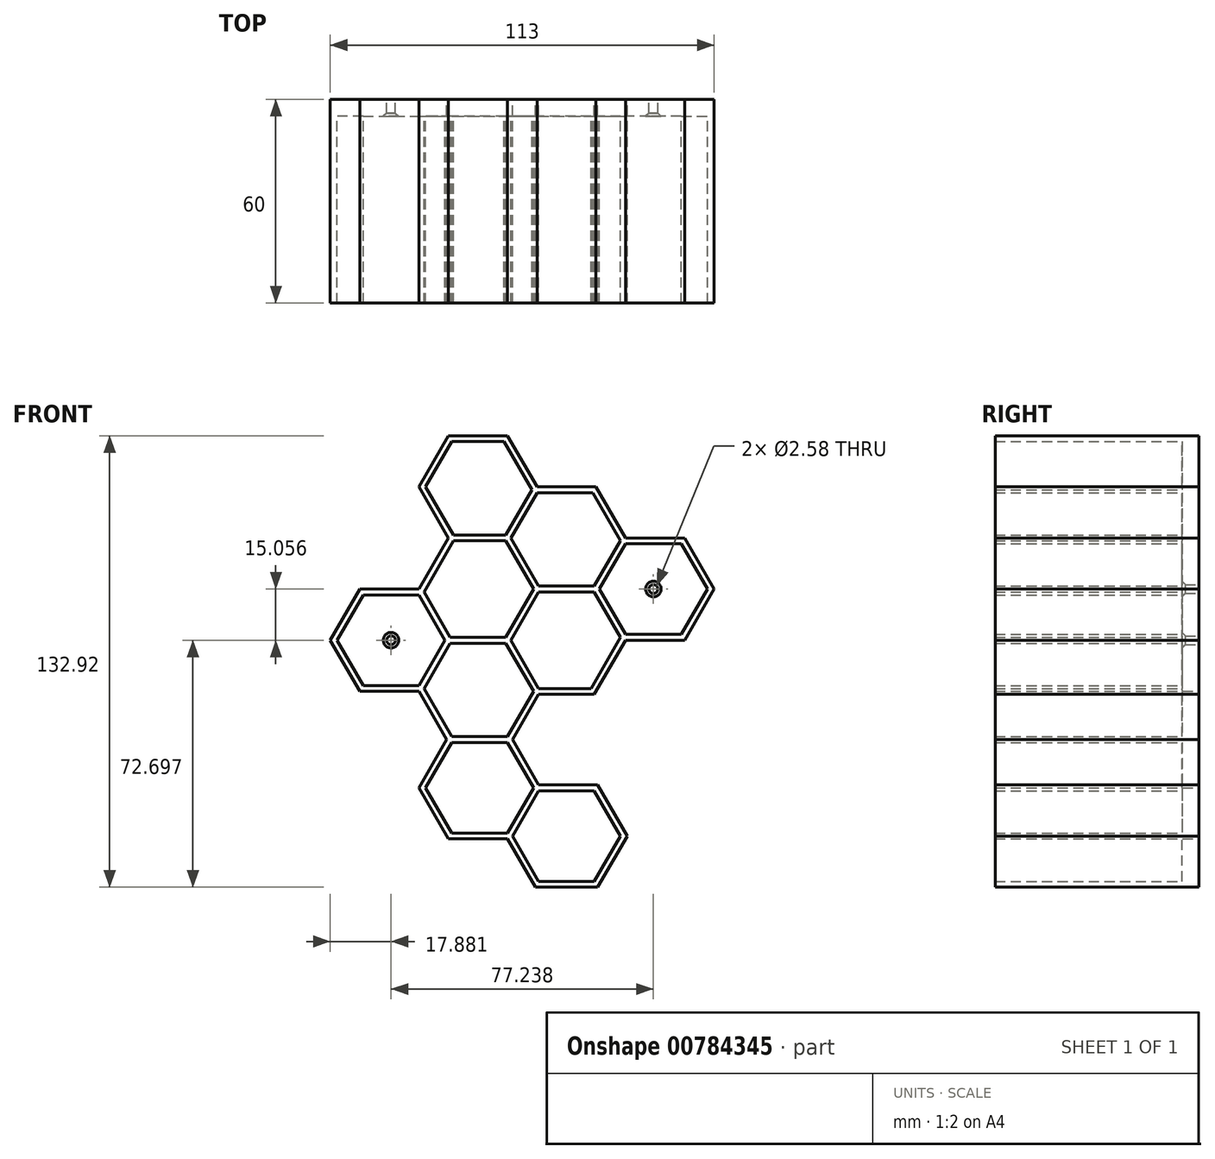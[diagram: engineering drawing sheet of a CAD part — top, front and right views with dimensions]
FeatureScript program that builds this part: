
annotation { "Feature Type Name" : "Feature", "Feature Type Description" : "" }
export const myFeature = defineFeature(function(context is Context, id is Id, definition is map)
    precondition{}
    {
        {
            var Q0;
            Q0=qCreatedBy(makeId("Front.planeOp"),FACE);
            var sketch = newSketch(context, id + "F0", { "sketchPlane" : qUnion([Q0])});
            skLineSegment(sketch, "E0.2", {"start": v(-21.73, -39.87) * mm, "end": v(-30.42, -24.82) * mm});
            skLineSegment(sketch, "E1.3", {"start": v(-30.42, 5.3) * mm, "end": v(-21.73, 20.35) * mm});
            skPoint(sketch, "E1.0.midPoint", {"position": v(0, -2.23) * mm});
            skLineSegment(sketch, "E2.3", {"start": v(30.42, -9.76) * mm, "end": v(21.73, -24.82) * mm});
            skLineSegment(sketch, "E3.4", {"start": v(4.35, 35.4) * mm, "end": v(21.73, 35.4) * mm});
            skLineSegment(sketch, "E3.5", {"start": v(21.73, 35.4) * mm, "end": v(30.42, 20.35) * mm});
            skLineSegment(sketch, "E4.0", {"start": v(56.5, 5.3) * mm, "end": v(47.8, -9.76) * mm});
            skLineSegment(sketch, "E4.1", {"start": v(47.8, -9.76) * mm, "end": v(30.42, -9.76) * mm});
            skLineSegment(sketch, "E4.4", {"start": v(30.42, 20.35) * mm, "end": v(47.8, 20.35) * mm});
            skLineSegment(sketch, "E4.5", {"start": v(47.8, 20.35) * mm, "end": v(56.5, 5.3) * mm});
            skLineSegment(sketch, "E5.2", {"start": v(-21.73, 20.35) * mm, "end": v(-30.42, 35.4) * mm});
            skLineSegment(sketch, "E5.3", {"start": v(-30.42, 35.4) * mm, "end": v(-21.73, 50.46) * mm});
            skLineSegment(sketch, "E5.4", {"start": v(-21.73, 50.46) * mm, "end": v(-4.35, 50.46) * mm});
            skLineSegment(sketch, "E5.5", {"start": v(-4.35, 50.46) * mm, "end": v(4.35, 35.4) * mm});
            skLineSegment(sketch, "E6.2", {"start": v(-30.42, -24.82) * mm, "end": v(-47.8, -24.82) * mm});
            skLineSegment(sketch, "E6.3", {"start": v(-47.8, -24.82) * mm, "end": v(-56.5, -9.76) * mm});
            skLineSegment(sketch, "E6.4", {"start": v(-56.5, -9.76) * mm, "end": v(-47.8, 5.3) * mm});
            skLineSegment(sketch, "E6.5", {"start": v(-47.8, 5.3) * mm, "end": v(-30.42, 5.3) * mm});
            skLineSegment(sketch, "E7.0", {"start": v(-28.44, 35.4) * mm, "end": v(-20.74, 48.74) * mm});
            skLineSegment(sketch, "E7.3", {"start": v(-46.81, 3.57) * mm, "end": v(-30.42, 3.57) * mm});
            skLineSegment(sketch, "E7.4", {"start": v(-54.51, -9.76) * mm, "end": v(-46.81, 3.57) * mm});
            skLineSegment(sketch, "E7.5", {"start": v(-20.74, 48.74) * mm, "end": v(-5.34, 48.74) * mm});
            skLineSegment(sketch, "E7.6", {"start": v(-46.81, -23.1) * mm, "end": v(-54.51, -9.76) * mm});
            skLineSegment(sketch, "E7.8", {"start": v(-20.74, -38.15) * mm, "end": v(-28.93, -23.96) * mm});
            skLineSegment(sketch, "E7.13", {"start": v(20.74, 33.68) * mm, "end": v(28.93, 19.49) * mm});
            skLineSegment(sketch, "E7.15", {"start": v(-5.34, 48.74) * mm, "end": v(2.86, 34.54) * mm});
            skLineSegment(sketch, "E7.16", {"start": v(46.81, 18.63) * mm, "end": v(54.51, 5.3) * mm});
            skLineSegment(sketch, "E7.17", {"start": v(54.51, 5.3) * mm, "end": v(46.81, -8.04) * mm});
            skLineSegment(sketch, "E7.18", {"start": v(46.81, -8.04) * mm, "end": v(30.42, -8.04) * mm});
            skLineSegment(sketch, "E8.2", {"start": v(3.35, 5.3) * mm, "end": v(-4.84, 19.49) * mm});
            skLineSegment(sketch, "E8.3", {"start": v(3.35, 5.3) * mm, "end": v(-4.84, -8.9) * mm});
            skLineSegment(sketch, "E8.4", {"start": v(-4.84, -8.9) * mm, "end": v(-21.23, -8.9) * mm});
            skLineSegment(sketch, "E9.0", {"start": v(-4.84, 21.2) * mm, "end": v(2.86, 34.54) * mm});
            skLineSegment(sketch, "E10.0", {"start": v(-3.35, 20.35) * mm, "end": v(4.35, 33.68) * mm});
            skLineSegment(sketch, "E10.1", {"start": v(4.84, 6.15) * mm, "end": v(-3.35, 20.35) * mm});
            skLineSegment(sketch, "E10.2", {"start": v(4.84, 6.15) * mm, "end": v(21.23, 6.15) * mm});
            skLineSegment(sketch, "E10.3", {"start": v(21.23, 6.15) * mm, "end": v(28.93, 19.49) * mm});
            skLineSegment(sketch, "E11.0", {"start": v(22.72, 5.3) * mm, "end": v(30.42, 18.63) * mm});
            skLineSegment(sketch, "E11.1", {"start": v(22.72, 5.3) * mm, "end": v(30.42, -8.04) * mm});
            skLineSegment(sketch, "E12.0", {"start": v(21.23, 4.43) * mm, "end": v(28.93, -8.9) * mm});
            skLineSegment(sketch, "E12.2", {"start": v(-3.35, -9.76) * mm, "end": v(4.84, -23.96) * mm});
            skLineSegment(sketch, "E12.3", {"start": v(4.84, 4.43) * mm, "end": v(-3.35, -9.76) * mm});
            skLineSegment(sketch, "E12.4", {"start": v(4.84, 4.43) * mm, "end": v(21.23, 4.43) * mm});
            skLineSegment(sketch, "E13.0", {"start": v(-22.72, -9.76) * mm, "end": v(-30.42, -23.1) * mm});
            skLineSegment(sketch, "E14.0", {"start": v(-21.23, -10.62) * mm, "end": v(-28.93, -23.96) * mm});
            skLineSegment(sketch, "E14.1", {"start": v(-4.84, -10.62) * mm, "end": v(-21.23, -10.62) * mm});
            skLineSegment(sketch, "E14.2", {"start": v(-4.84, -10.62) * mm, "end": v(3.35, -24.82) * mm});
            skLineSegment(sketch, "E14.3", {"start": v(3.35, -24.82) * mm, "end": v(-4.35, -38.15) * mm});
            skLineSegment(sketch, "E15.1", {"start": v(4.84, -25.68) * mm, "end": v(20.24, -25.68) * mm});
            skPoint(sketch, "E16", {"position": v(12.8, 19.92) * mm});
            skLineSegment(sketch, "E17", {"start": v(-0.75, -1.8) * mm, "end": v(0.75, -2.67) * mm, "construction": true});
            skLineSegment(sketch, "E18", {"start": v(30.42, 18.63) * mm, "end": v(46.81, 18.63) * mm});
            skLineSegment(sketch, "E19", {"start": v(28.93, -8.9) * mm, "end": v(20.24, -23.96) * mm});
            skLineSegment(sketch, "E20", {"start": v(20.24, -23.96) * mm, "end": v(4.84, -23.96) * mm});
            skLineSegment(sketch, "E21", {"start": v(-4.35, -38.15) * mm, "end": v(-20.74, -38.15) * mm});
            skLineSegment(sketch, "E22", {"start": v(-30.42, -23.1) * mm, "end": v(-46.81, -23.1) * mm});
            skLineSegment(sketch, "E23", {"start": v(-30.42, 3.57) * mm, "end": v(-22.72, -9.76) * mm});
            skLineSegment(sketch, "E24", {"start": v(-28.93, 4.43) * mm, "end": v(-21.23, -8.9) * mm});
            skLineSegment(sketch, "E25", {"start": v(-28.93, 4.43) * mm, "end": v(-20.24, 19.49) * mm});
            skLineSegment(sketch, "E26", {"start": v(-20.24, 21.2) * mm, "end": v(-28.44, 35.4) * mm});
            skLineSegment(sketch, "E27", {"start": v(-20.24, 21.2) * mm, "end": v(-4.84, 21.2) * mm});
            skLineSegment(sketch, "E28", {"start": v(-20.24, 19.49) * mm, "end": v(-4.84, 19.49) * mm});
            skLineSegment(sketch, "E29", {"start": v(4.35, 33.68) * mm, "end": v(20.74, 33.68) * mm});
            skLineSegment(sketch, "E30", {"start": v(46.81, 18.63) * mm, "end": v(30.42, -8.04) * mm, "construction": true});
            skLineSegment(sketch, "E31", {"start": v(-30.42, 3.57) * mm, "end": v(-46.81, -23.1) * mm, "construction": true});
            skLineSegment(sketch, "E32", {"start": v(-21.23, -10.62) * mm, "end": v(-20.74, -9.76) * mm, "construction": true});
            skLineSegment(sketch, "E33", {"start": v(-21.23, -8.9) * mm, "end": v(-20.74, -9.76) * mm, "construction": true});
            skLineSegment(sketch, "E34", {"start": v(-30.42, -24.82) * mm, "end": v(-29.43, -24.82) * mm, "construction": true});
            skLineSegment(sketch, "E35", {"start": v(-28.44, -24.82) * mm, "end": v(-28.93, -23.96) * mm, "construction": true});
            skLineSegment(sketch, "E36", {"start": v(-28.93, -23.96) * mm, "end": v(-29.43, -24.82) * mm, "construction": true});
            skPoint(sketch, "E37", {"position": v(-29.43, -24.82) * mm});
            skPoint(sketch, "E38", {"position": v(-20.74, -9.76) * mm});
            skLineSegment(sketch, "E39", {"start": v(-20.74, -9.76) * mm, "end": v(-20.24, -10.62) * mm, "construction": true});
            skLineSegment(sketch, "E40", {"start": v(-20.74, -9.76) * mm, "end": v(-20.24, -8.9) * mm, "construction": true});
            skLineSegment(sketch, "E41", {"start": v(-29.43, -24.82) * mm, "end": v(-28.44, -24.82) * mm, "construction": true});
            skLineSegment(sketch, "E42", {"start": v(-29.43, -24.82) * mm, "end": v(-29.93, -25.68) * mm, "construction": true});
            skLineSegment(sketch, "E43", {"start": v(-30.42, 5.3) * mm, "end": v(-29.43, 5.3) * mm, "construction": true});
            skLineSegment(sketch, "E44", {"start": v(-28.93, 4.43) * mm, "end": v(-29.93, 6.15) * mm, "construction": true});
            skLineSegment(sketch, "E45", {"start": v(-29.43, 5.3) * mm, "end": v(-28.44, 5.3) * mm, "construction": true});
            skLineSegment(sketch, "E46", {"start": v(20.24, -25.68) * mm, "end": v(21.23, -25.68) * mm});
            skLineSegment(sketch, "E47", {"start": v(21.73, -24.82) * mm, "end": v(21.23, -25.68) * mm});
            skPoint(sketch, "E48", {"position": v(-3.27, -37.05) * mm});
            skLineSegment(sketch, "E49", {"start": v(-4.35, -38.15) * mm, "end": v(-3.35, -39.87) * mm, "construction": true});
            skLineSegment(sketch, "E50", {"start": v(-47.8, 5.3) * mm, "end": v(-46.81, 3.57) * mm, "construction": true});
            skLineSegment(sketch, "E51", {"start": v(-21.73, -39.87) * mm, "end": v(-3.35, -39.87) * mm});
            skLineSegment(sketch, "E52", {"start": v(-3.35, -39.87) * mm, "end": v(4.84, -25.68) * mm});
            skPoint(sketch, "E53", {"position": v(-13.94, -39.01) * mm});
            skLineSegment(sketch, "E54", {"start": v(-13.94, -39.01) * mm, "end": v(-22.23, -39.01) * mm, "construction": true});
            skLineSegment(sketch, "E55", {"start": v(-13.94, -39.01) * mm, "end": v(-2.86, -39.01) * mm, "construction": true});
            skLineSegment(sketch, "E56.2", {"start": v(-4.35, -68.26) * mm, "end": v(-21.73, -68.26) * mm});
            skLineSegment(sketch, "E56.3", {"start": v(-21.73, -68.26) * mm, "end": v(-30.42, -53.2) * mm});
            skLineSegment(sketch, "E56.4", {"start": v(-30.42, -53.2) * mm, "end": v(-21.73, -38.15) * mm});
            skLineSegment(sketch, "E56.5", {"start": v(-21.73, -38.15) * mm, "end": v(-4.35, -38.15) * mm});
            skLineSegment(sketch, "E57.3", {"start": v(-20.74, -39.87) * mm, "end": v(-4.35, -39.87) * mm});
            skLineSegment(sketch, "E57.4", {"start": v(-28.44, -53.2) * mm, "end": v(-20.74, -39.87) * mm});
            skLineSegment(sketch, "E57.6", {"start": v(-20.74, -66.54) * mm, "end": v(-28.44, -53.2) * mm});
            skLineSegment(sketch, "E58.0", {"start": v(3.35, -53.2) * mm, "end": v(-4.35, -66.54) * mm});
            skLineSegment(sketch, "E59.0", {"start": v(4.84, -54.07) * mm, "end": v(-2.86, -67.4) * mm});
            skLineSegment(sketch, "E60", {"start": v(-4.35, -66.54) * mm, "end": v(-20.74, -66.54) * mm});
            skLineSegment(sketch, "E61", {"start": v(-4.35, -39.87) * mm, "end": v(3.35, -53.2) * mm});
            skLineSegment(sketch, "E62", {"start": v(-2.86, -39.01) * mm, "end": v(4.84, -52.35) * mm});
            skLineSegment(sketch, "E63", {"start": v(-4.43, -42.7) * mm, "end": v(-20.82, -69.36) * mm, "construction": true});
            skLineSegment(sketch, "E64", {"start": v(4.84, -54.07) * mm, "end": v(5.34, -53.2) * mm});
            skLineSegment(sketch, "E65", {"start": v(4.84, -52.35) * mm, "end": v(5.34, -53.2) * mm});
            skLineSegment(sketch, "E66", {"start": v(-4.35, -68.26) * mm, "end": v(-3.35, -68.26) * mm});
            skLineSegment(sketch, "E67", {"start": v(-2.86, -67.4) * mm, "end": v(-3.35, -68.26) * mm});
            skLineSegment(sketch, "E68", {"start": v(-4.35, -38.15) * mm, "end": v(-3.35, -38.15) * mm});
            skLineSegment(sketch, "E69", {"start": v(-2.86, -39.01) * mm, "end": v(-3.35, -38.15) * mm});
            skPoint(sketch, "E70", {"position": v(-22.23, -39.01) * mm});
            skLineSegment(sketch, "E71", {"start": v(-22.23, -39.01) * mm, "end": v(-2.86, -39.01) * mm, "construction": true});
            skLineSegment(sketch, "E72", {"start": v(4.84, -52.35) * mm, "end": v(-4.35, -68.26) * mm, "construction": true});
            skLineSegment(sketch, "E73.2", {"start": v(21.23, -82.46) * mm, "end": v(3.85, -82.46) * mm});
            skLineSegment(sketch, "E73.3", {"start": v(3.85, -82.46) * mm, "end": v(-4.84, -67.4) * mm});
            skLineSegment(sketch, "E73.4", {"start": v(-4.84, -67.4) * mm, "end": v(3.85, -52.35) * mm});
            skLineSegment(sketch, "E73.5", {"start": v(3.85, -52.35) * mm, "end": v(21.23, -52.35) * mm});
            skLineSegment(sketch, "E74.3", {"start": v(4.84, -54.07) * mm, "end": v(21.23, -54.07) * mm});
            skLineSegment(sketch, "E74.4", {"start": v(-2.86, -67.4) * mm, "end": v(4.84, -54.07) * mm});
            skLineSegment(sketch, "E74.6", {"start": v(4.84, -80.74) * mm, "end": v(-2.86, -67.4) * mm});
            skLineSegment(sketch, "E75.0", {"start": v(28.93, -67.4) * mm, "end": v(21.23, -80.74) * mm});
            skLineSegment(sketch, "E76.0", {"start": v(30.42, -68.26) * mm, "end": v(22.72, -81.6) * mm});
            skLineSegment(sketch, "E77", {"start": v(21.23, -80.74) * mm, "end": v(4.84, -80.74) * mm});
            skLineSegment(sketch, "E78", {"start": v(21.23, -54.07) * mm, "end": v(28.93, -67.4) * mm});
            skLineSegment(sketch, "E79", {"start": v(22.72, -53.2) * mm, "end": v(30.42, -66.54) * mm});
            skLineSegment(sketch, "E80", {"start": v(21.23, -54.07) * mm, "end": v(4.84, -80.74) * mm, "construction": true});
            skLineSegment(sketch, "E81", {"start": v(30.42, -68.26) * mm, "end": v(30.92, -67.4) * mm});
            skLineSegment(sketch, "E82", {"start": v(30.42, -66.54) * mm, "end": v(30.92, -67.4) * mm});
            skLineSegment(sketch, "E83", {"start": v(21.23, -82.46) * mm, "end": v(22.23, -82.46) * mm});
            skLineSegment(sketch, "E84", {"start": v(22.72, -81.6) * mm, "end": v(22.23, -82.46) * mm});
            skLineSegment(sketch, "E85", {"start": v(21.23, -52.35) * mm, "end": v(22.23, -52.35) * mm});
            skLineSegment(sketch, "E86", {"start": v(22.72, -53.2) * mm, "end": v(22.23, -52.35) * mm});
            skLineSegment(sketch, "E87", {"start": v(-4.35, -66.54) * mm, "end": v(-5.34, -68.26) * mm, "construction": true});
            skPoint(sketch, "E88", {"position": v(4.84, -52.35) * mm});
            skPoint(sketch, "E89", {"position": v(-4.35, -68.26) * mm});
            skPoint(sketch, "E90", {"position": v(-38.62, -9.76) * mm});
            skPoint(sketch, "E91", {"position": v(38.62, 5.3) * mm});
            skCircle(sketch, "E92", {"center": v(38.62, 5.3) * mm, "radius": 1.3 * mm});
            skCircle(sketch, "E93", {"center": v(-38.62, -9.76) * mm, "radius": 1.3 * mm});
            skSolve(sketch);
        }
        {
            var Q0;
            Q0=makeQuery(id+"F0.imprint","IMPRINT",FACE,{"disambiguationData":[TD([[makeQuery(id+"F0.imprint","IMPRINT",EDGE,{"derivedFrom":sQuery(id+"F0.wireOp",EDGE,"E1.3")}),-1.0]])]});
            var Q1;
            {var subQ2=sQuery(id+"F0.wireOp",EDGE,"E61");Q1=makeQuery(id+"F0.imprint","IMPRINT",FACE,{"disambiguationData":[TD([[makeQuery(id+"F0.imprint","IMPRINT",EDGE,{"derivedFrom":subQ2}),1.0]])]});}
            var Q2;
            Q2=makeQuery(id+"F0.imprint","IMPRINT",FACE,{"disambiguationData":[TD([[makeQuery(id+"F0.imprint","IMPRINT",EDGE,{"derivedFrom":sQuery(id+"F0.wireOp",EDGE,"E21")}),1.0]])]});
            var Q3;
            {var subQ0=sQuery(id+"F0.wireOp",EDGE,"E56.2");Q3=makeQuery(id+"F0.imprint","IMPRINT",FACE,{"disambiguationData":[TD([[makeQuery(id+"F0.imprint","IMPRINT",EDGE,{"derivedFrom":subQ0}),-1.0]])]});}
            var Q4;
            {var subQ4=sQuery(id+"F0.wireOp",EDGE,"E58.0");Q4=makeQuery(id+"F0.imprint","IMPRINT",FACE,{"disambiguationData":[TD([[makeQuery(id+"F0.imprint","IMPRINT",EDGE,{"derivedFrom":subQ4}),1.0]])]});}
            var Q5;
            Q5=makeQuery(id+"F0.imprint","IMPRINT",FACE,{"disambiguationData":[TD([[makeQuery(id+"F0.imprint","IMPRINT",EDGE,{"derivedFrom":sQuery(id+"F0.wireOp",EDGE,"E64")}),-1.0]])]});
            extrude(context, id + "F1", {"entities" : qUnion([Q0, Q1, Q2, Q3, Q4, Q5]), "depth" : 60 * mm, "offsetDistance" : 25 * mm});
        }
        {
            var Q0;
            Q0=makeQuery(id+"F0.imprint","IMPRINT",FACE,{"disambiguationData":[TD([[makeQuery(id+"F0.imprint","IMPRINT",EDGE,{"derivedFrom":sQuery(id+"F0.wireOp",EDGE,"E7.8")}),-1.0]])]});
            var Q1;
            Q1=makeQuery(id+"F0.imprint","IMPRINT",FACE,{"disambiguationData":[TD([[makeQuery(id+"F0.imprint","IMPRINT",EDGE,{"derivedFrom":sQuery(id+"F0.wireOp",EDGE,"E7.3")}),-1.0]])]});
            var Q2;
            Q2=makeQuery(id+"F0.imprint","IMPRINT",FACE,{"disambiguationData":[TD([[makeQuery(id+"F0.imprint","IMPRINT",EDGE,{"derivedFrom":sQuery(id+"F0.wireOp",EDGE,"E8.2")}),1.0]])]});
            var Q3;
            Q3=makeQuery(id+"F0.imprint","IMPRINT",FACE,{"disambiguationData":[TD([[makeQuery(id+"F0.imprint","IMPRINT",EDGE,{"derivedFrom":sQuery(id+"F0.wireOp",EDGE,"E12.0")}),-1.0]])]});
            var Q4;
            Q4=makeQuery(id+"F0.imprint","IMPRINT",FACE,{"disambiguationData":[TD([[makeQuery(id+"F0.imprint","IMPRINT",EDGE,{"derivedFrom":sQuery(id+"F0.wireOp",EDGE,"E7.13")}),-1.0]])]});
            var Q5;
            Q5=makeQuery(id+"F0.imprint","IMPRINT",FACE,{"disambiguationData":[TD([[makeQuery(id+"F0.imprint","IMPRINT",EDGE,{"derivedFrom":sQuery(id+"F0.wireOp",EDGE,"E7.16")}),-1.0]])]});
            var Q6;
            Q6=makeQuery(id+"F0.imprint","IMPRINT",FACE,{"disambiguationData":[TD([[makeQuery(id+"F0.imprint","IMPRINT",EDGE,{"derivedFrom":sQuery(id+"F0.wireOp",EDGE,"E7.0")}),-1.0]])]});
            var Q7;
            {var subQ0=sQuery(id+"F0.wireOp",EDGE,"E57.4");Q7=makeQuery(id+"F0.imprint","IMPRINT",FACE,{"disambiguationData":[TD([[makeQuery(id+"F0.imprint","IMPRINT",EDGE,{"derivedFrom":subQ0}),-1.0]])]});}
            var Q8;
            Q8=makeQuery(id+"F0.imprint","IMPRINT",FACE,{"disambiguationData":[TD([[makeQuery(id+"F0.imprint","IMPRINT",EDGE,{"derivedFrom":sQuery(id+"F0.wireOp",EDGE,"E59.0")}),1.0]])]});
            extrude(context, id + "F2", {"entities" : qUnion([Q0, Q1, Q2, Q3, Q4, Q5, Q6, Q7, Q8]), "operationType" : NewBodyOperationType.ADD, "depth" : 5 * mm, "offsetDistance" : 25 * mm});
        }
        {
            var Q0;
            Q0=makeQuery(id+"F2.opExtrude","CAP_EDGE",EDGE,{"disambiguationData":[OSD([sQuery(id+"F0.wireOp",EDGE,"E93")])],"isStart":false});
            var Q1;
            Q1=makeQuery(id+"F2.opExtrude","CAP_EDGE",EDGE,{"disambiguationData":[OSD([sQuery(id+"F0.wireOp",EDGE,"E92")])],"isStart":false});
            chamfer(context, id + "F3", {"entities" : qUnion([Q0, Q1]), "width" : 1 * mm, "tangentPropagation" : true});
        }
    });
